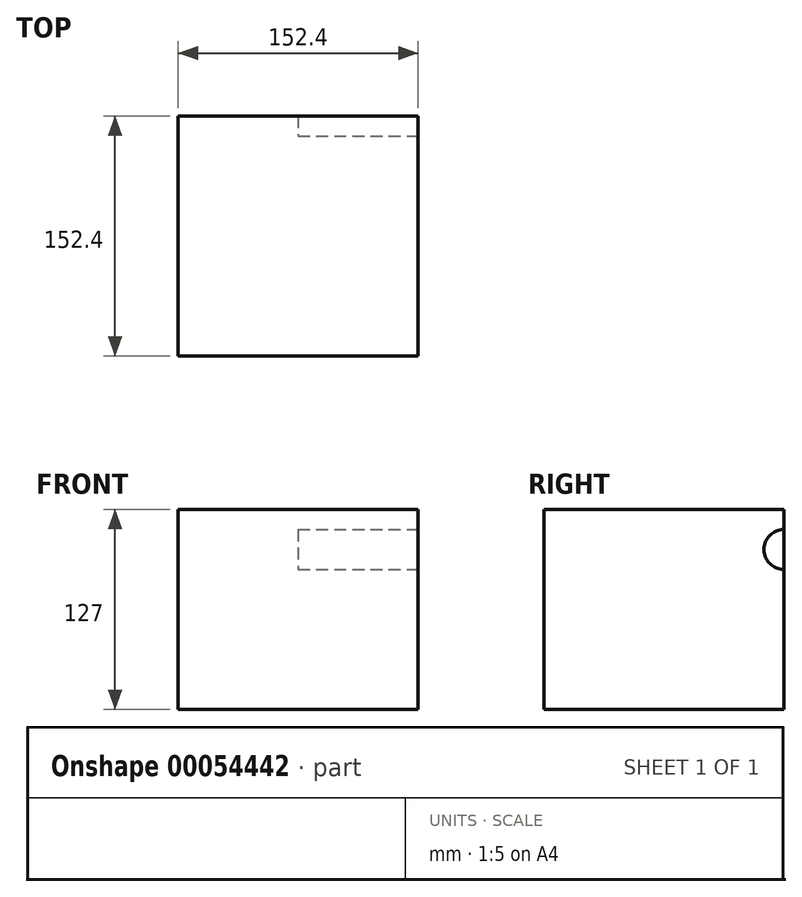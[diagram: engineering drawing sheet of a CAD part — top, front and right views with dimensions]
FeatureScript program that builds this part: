
annotation { "Feature Type Name" : "Feature", "Feature Type Description" : "" }
export const myFeature = defineFeature(function(context is Context, id is Id, definition is map)
    precondition{}
    {
        {
            var Q0;
            Q0=qCreatedBy(makeId("Top.planeOp"),FACE);
            var sketch = newSketch(context, id + "F0", { "sketchPlane" : qUnion([Q0])});
            skLineSegment(sketch, "E0.rect.bottom", {"start": v(-76.2, 76.2) * mm, "end": v(76.2, 76.2) * mm});
            skLineSegment(sketch, "E0.rect.top", {"start": v(-76.2, -76.2) * mm, "end": v(76.2, -76.2) * mm});
            skLineSegment(sketch, "E0.rect.left", {"start": v(-76.2, 76.2) * mm, "end": v(-76.2, -76.2) * mm});
            skLineSegment(sketch, "E0.rect.right", {"start": v(76.2, 76.2) * mm, "end": v(76.2, -76.2) * mm});
            skPoint(sketch, "E0.rect.middle", {"position": v(0, 0) * mm});
            skSolve(sketch);
        }
        {
            var Q0;
            Q0 = qSketchRegion(id + "F0", true);
            extrude(context, id + "F1", {"entities" : qUnion([Q0]), "endBound" : BoundingType.SYMMETRIC, "depth" : 127 * mm});
        }
        {
            var Q0;
            Q0=makeQuery(id+"F1.opExtrude","SWEPT_FACE",FACE,{"disambiguationData":[OSD([sQuery(id+"F0.wireOp",EDGE,"E0.rect.right")])]});
            var sketch = newSketch(context, id + "F2", { "sketchPlane" : qUnion([Q0])});
            skCircle(sketch, "E1", {"center": v(76.2, 38.1) * mm, "radius": 12.7 * mm});
            skSolve(sketch);
        }
        {
            var Q0;
            {var subQ0=sQuery(id+"F2.wireOp",EDGE,"E1");var subQ1=makeQuery(id+"F1.opExtrude","SWEPT_EDGE",EDGE,{"disambiguationData":[OSD([sQuery(id+"F0.wireOp",EDGE,"E0.rect.bottom"),sQuery(id+"F0.wireOp",EDGE,"E0.rect.right")])]});var subQ2=makeQuery(id+"F2.imprint","INTERSECT",VERTEX,{"disambiguationData":[OD(0.0)],"derivedFrom":[subQ1,subQ0]});Q0=makeQuery(id+"F2.imprint","IMPRINT",FACE,{"disambiguationData":[TD([[makeQuery(id+"F2.imprint","IMPRINT",EDGE,{"disambiguationData":[TD([[subQ2,-1.0]])],"derivedFrom":subQ0}),1.0]])]});}
            var Q1;
            {var subQ0=sQuery(id+"F2.wireOp",EDGE,"E1");var subQ1=makeQuery(id+"F1.opExtrude","SWEPT_EDGE",EDGE,{"disambiguationData":[OSD([sQuery(id+"F0.wireOp",EDGE,"E0.rect.bottom"),sQuery(id+"F0.wireOp",EDGE,"E0.rect.right")])]});var subQ2=makeQuery(id+"F2.imprint","INTERSECT",VERTEX,{"disambiguationData":[OD(0.0)],"derivedFrom":[subQ1,subQ0]});Q1=makeQuery(id+"F2.imprint","IMPRINT",FACE,{"disambiguationData":[TD([[makeQuery(id+"F2.imprint","IMPRINT",EDGE,{"disambiguationData":[TD([[subQ2,1.0]])],"derivedFrom":subQ0}),1.0]])]});}
            extrude(context, id + "F3", {"entities" : qUnion([Q0, Q1]), "operationType" : NewBodyOperationType.REMOVE, "oppositeDirection" : true, "depth" : 76.2 * mm});
        }
    });
